# Revit family: Haworth_Pergola_Panel_Post NEW
name_source: partatom
category: Furniture Systems
revit_build: Autodesk Revit 2018 (Build: 20170223_1515(x64)
units: mm (PartAtom-declared; Revit-internal decimal feet)

## family parameters
Always vertical = Yes
Cut with Voids When Loaded = No
OmniClass Number = 23.40.70.14.64.21
OmniClass Title = Systems Furniture
Part Type = Normal
Room Calculation Point = No
Round Connector Dimension = Use Diameter
Shared = No
Work Plane-Based = No

## types (4) — shared parameters
2-Way Void Dim. = 95 1/2"
Actual Depth = 4"
Actual Height = 96"
Actual Width = 4"
Assembly Code = E2020200
Base Height = 1/2"
Description = Haworth - Pergola Panel - Post
Glide Finish = Haworth _ Polymer _ Black
Manufacturer = Haworth
Max. Height = 96"
Max. Width = 3"
Min. Height = 96"
Min. Width = 3"
Model = Haworth Pergola
Post Finish = Haworth _ Paint _ Undecided _ Pergola
Revision Number = 1
Size = Verify Final Dim. w/ Haworth
Sustainability Info = http://www.haworth.com
Top Trim Width = 1/2"
Trim Finish = Haworth _ Paint _ Undecided _ Pergola
URL = http://www.haworth.com
URL - Product = https://www.haworth.com
Underbeam Height = 91 103/128"
Warranty = http://www.haworth.com

## per-type parameters (varying)
| type | 2Way Post | 3-Way Void Dim. | 3Way Post | 4-Way Void Dim. | 4Way Post | Standard Post | Underbeam |
| 2-Way Connector | Yes | 1/2" | No | 1/2" | No | Yes | No |
| 3-Way Connector | No | 95 1/2" | Yes | 1/2" | No | Yes | No |
| 4-Way Connector | No | 95 1/2" | No | 95 1/2" | Yes | Yes | No |
| Underbeam EOR | No | 95 1/2" | No | 1/2" | No | No | Yes |

## geometry (parser evidence)
native form markers: Sweep x3
no freeform markers — native parametric forms only
